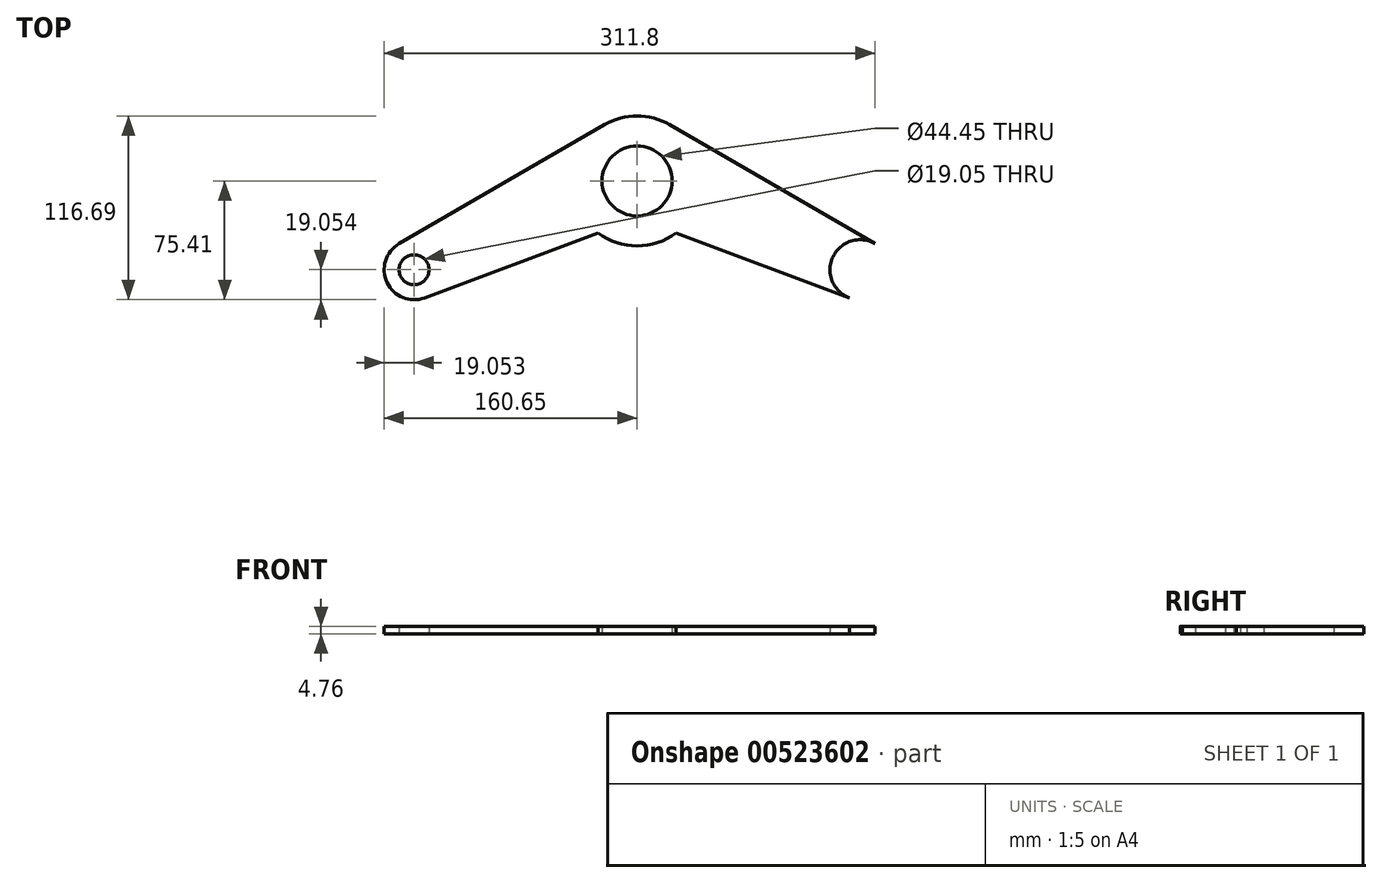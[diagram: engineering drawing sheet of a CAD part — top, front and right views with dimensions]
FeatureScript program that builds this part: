
annotation { "Feature Type Name" : "Feature", "Feature Type Description" : "" }
export const myFeature = defineFeature(function(context is Context, id is Id, definition is map)
    precondition{}
    {
        {
            var Q0;
            Q0=qCreatedBy(makeId("Top.planeOp"),FACE);
            var sketch = newSketch(context, id + "F0", { "sketchPlane" : qUnion([Q0])});
            skCircle(sketch, "E0", {"center": v(0, 0) * mm, "radius": 22.23 * mm});
            skCircle(sketch, "E1", {"center": v(0, 0) * mm, "radius": 41.28 * mm});
            skLineSegment(sketch, "E2", {"start": v(-151.15, -39.87) * mm, "end": v(-20.7, 35.71) * mm});
            skLineSegment(sketch, "E3.MirrorCS", {"start": v(-134.92, -74.2) * mm, "end": v(-24.79, -33) * mm});
            skLineSegment(sketch, "E4.MirrorCS", {"start": v(151.15, -39.87) * mm, "end": v(20.7, 35.71) * mm});
            skLineSegment(sketch, "E5.MirrorCS", {"start": v(134.92, -74.2) * mm, "end": v(24.79, -33) * mm});
            skLineSegment(sketch, "E6", {"start": v(0, 98.43) * mm, "end": v(-203.2, 98.42) * mm, "construction": true});
            skCircle(sketch, "E7", {"center": v(0, 0) * mm, "radius": 152.4 * mm, "construction": true});
            skLineSegment(sketch, "E8", {"start": v(-203.2, 98.43) * mm, "end": v(-141.6, -56.36) * mm, "construction": true});
            skCircle(sketch, "E9", {"center": v(-141.6, -56.36) * mm, "radius": 19.05 * mm});
            skCircle(sketch, "E10.MirrorC", {"center": v(141.6, -56.36) * mm, "radius": 19.05 * mm});
            skCircle(sketch, "E11", {"center": v(-141.6, -56.36) * mm, "radius": 9.53 * mm});
            skCircle(sketch, "E12.MirrorC", {"center": v(141.6, -56.36) * mm, "radius": 9.53 * mm});
            skSolve(sketch);
        }
        {
            var Q0;
            {var subQ0=sQuery(id+"F0.wireOp",EDGE,"E2");Q0=makeQuery(id+"F0.imprint","IMPRINT",FACE,{"disambiguationData":[TD([[makeQuery(id+"F0.imprint","IMPRINT",EDGE,{"derivedFrom":subQ0}),-1.0]])]});}
            var Q1;
            Q1=makeQuery(id+"F0.imprint","IMPRINT",FACE,{"disambiguationData":[TD([[makeQuery(id+"F0.imprint","IMPRINT",EDGE,{"derivedFrom":sQuery(id+"F0.wireOp",EDGE,"E0")}),-1.0]])]});
            var Q2;
            {var subQ0=sQuery(id+"F0.wireOp",EDGE,"E4.MirrorCS");Q2=makeQuery(id+"F0.imprint","IMPRINT",FACE,{"disambiguationData":[TD([[makeQuery(id+"F0.imprint","IMPRINT",EDGE,{"derivedFrom":subQ0}),1.0]])]});}
            var Q3;
            {var subQ0=sQuery(id+"F0.wireOp",EDGE,"E9");var subQ1=makeQuery(id+"F0.imprint","INTERSECT",VERTEX,{"derivedFrom":[sQuery(id+"F0.wireOp",EDGE,"E2"),subQ0]});Q3=makeQuery(id+"F0.imprint","IMPRINT",FACE,{"disambiguationData":[TD([[makeQuery(id+"F0.imprint","IMPRINT",EDGE,{"disambiguationData":[TD([[subQ1,-1.0]])],"derivedFrom":subQ0}),1.0]])]});}
            var Q4;
            {var subQ0=sQuery(id+"F0.wireOp",EDGE,"E10.MirrorC");var subQ1=makeQuery(id+"F0.imprint","INTERSECT",VERTEX,{"derivedFrom":[sQuery(id+"F0.wireOp",EDGE,"E4.MirrorCS"),subQ0]});Q4=makeQuery(id+"F0.imprint","IMPRINT",FACE,{"disambiguationData":[TD([[makeQuery(id+"F0.imprint","IMPRINT",EDGE,{"disambiguationData":[TD([[subQ1,-1.0]])],"derivedFrom":subQ0}),-1.0]])]});}
            extrude(context, id + "F1", {"entities" : qUnion([Q0, Q1, Q2, Q3, Q4]), "depth" : 4.76 * mm, "offsetDistance" : 25.4 * mm});
        }
    });
